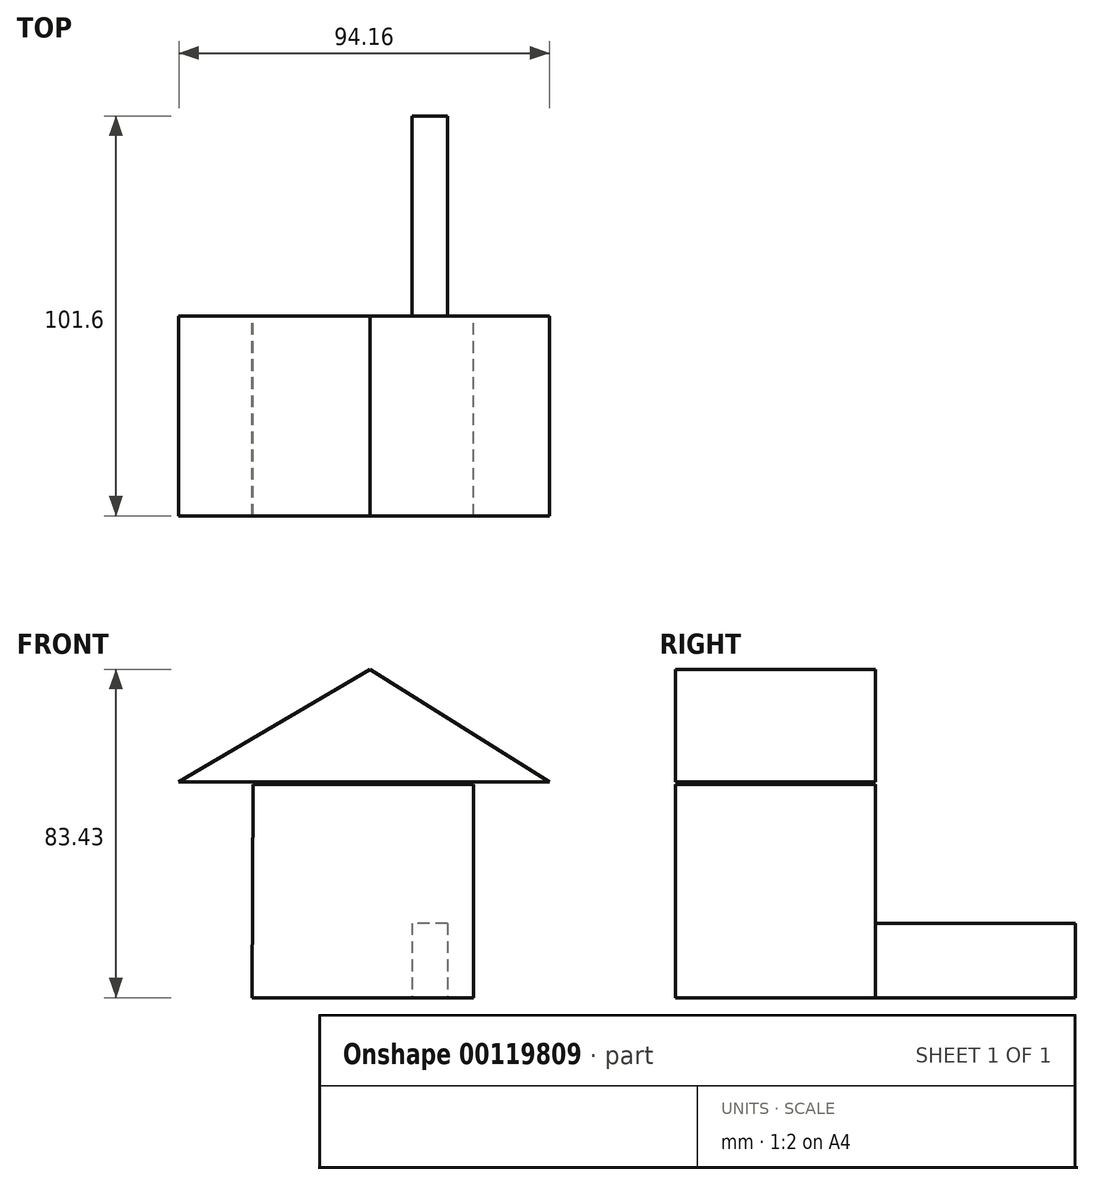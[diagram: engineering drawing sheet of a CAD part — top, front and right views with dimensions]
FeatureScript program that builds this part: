
annotation { "Feature Type Name" : "Feature", "Feature Type Description" : "" }
export const myFeature = defineFeature(function(context is Context, id is Id, definition is map)
    precondition{}
    {
        {
            var Q0;
            Q0=qCreatedBy(makeId("Front.planeOp"),FACE);
            var sketch = newSketch(context, id + "F0", { "sketchPlane" : qUnion([Q0])});
            skPoint(sketch, "E0.bottom.start.orphan", {"position": v(0, 76.43) * mm});
            skPoint(sketch, "E0.top.end.orphan", {"position": v(76.08, 0) * mm});
            skLineSegment(sketch, "E1", {"start": v(-21.96, 35.31) * mm, "end": v(34.06, 35.31) * mm});
            skLineSegment(sketch, "E2", {"start": v(34.06, 35.31) * mm, "end": v(34.06, -18.92) * mm});
            skLineSegment(sketch, "E3", {"start": v(34.06, -18.92) * mm, "end": v(-22.26, -18.92) * mm});
            skLineSegment(sketch, "E4", {"start": v(-22.26, -18.92) * mm, "end": v(-21.96, 35.31) * mm});
            skSolve(sketch);
        }
        {
            var Q0;
            Q0 = qSketchRegion(id + "F0", true);
            extrude(context, id + "F1", {"entities" : qUnion([Q0]), "depth" : 50.8 * mm});
        }
        {
            var Q0;
            Q0=qCreatedBy(makeId("Front.planeOp"),FACE);
            var sketch = newSketch(context, id + "F2", { "sketchPlane" : qUnion([Q0])});
            skLineSegment(sketch, "E5", {"start": v(-40.82, 35.9) * mm, "end": v(53.34, 35.9) * mm});
            skLineSegment(sketch, "E6", {"start": v(53.34, 35.9) * mm, "end": v(7.75, 64.51) * mm});
            skLineSegment(sketch, "E7", {"start": v(7.75, 64.51) * mm, "end": v(-40.82, 35.9) * mm});
            skSolve(sketch);
        }
        {
            var Q0;
            Q0=makeQuery(id+"F2.imprint","IMPRINT",FACE,{"disambiguationData":[TD([[makeQuery(id+"F2.imprint","IMPRINT",EDGE,{"derivedFrom":sQuery(id+"F2.wireOp",EDGE,"E5")}),1.0]])]});
            extrude(context, id + "F3", {"entities" : qUnion([Q0]), "depth" : 50.8 * mm});
        }
        {
            var Q0;
            Q0=makeQuery(id+"F1.opExtrude","CAP_FACE",FACE,{"disambiguationData":[OSD([sQuery(id+"F0.wireOp",EDGE,"E1"),sQuery(id+"F0.wireOp",EDGE,"E2"),sQuery(id+"F0.wireOp",EDGE,"E3"),sQuery(id+"F0.wireOp",EDGE,"E4")])],"isStart":true});
            var sketch = newSketch(context, id + "F4", { "sketchPlane" : qUnion([Q0])});
            skLineSegment(sketch, "E8.bottom", {"start": v(-27.41, 0) * mm, "end": v(-18.48, 0) * mm});
            skLineSegment(sketch, "E8.top", {"start": v(-27.41, -18.92) * mm, "end": v(-18.48, -18.92) * mm});
            skLineSegment(sketch, "E8.left", {"start": v(-27.41, 0) * mm, "end": v(-27.41, -18.92) * mm});
            skLineSegment(sketch, "E8.right", {"start": v(-18.48, 0) * mm, "end": v(-18.48, -18.92) * mm});
            skSolve(sketch);
        }
        {
            var Q0;
            Q0=makeQuery(id+"F4.imprint","IMPRINT",FACE,{"disambiguationData":[TD([[makeQuery(id+"F4.imprint","IMPRINT",EDGE,{"derivedFrom":sQuery(id+"F4.wireOp",EDGE,"E8.bottom")}),-1.0]])]});
            extrude(context, id + "F5", {"entities" : qUnion([Q0]), "operationType" : NewBodyOperationType.ADD, "depth" : 50.8 * mm});
        }
    });
